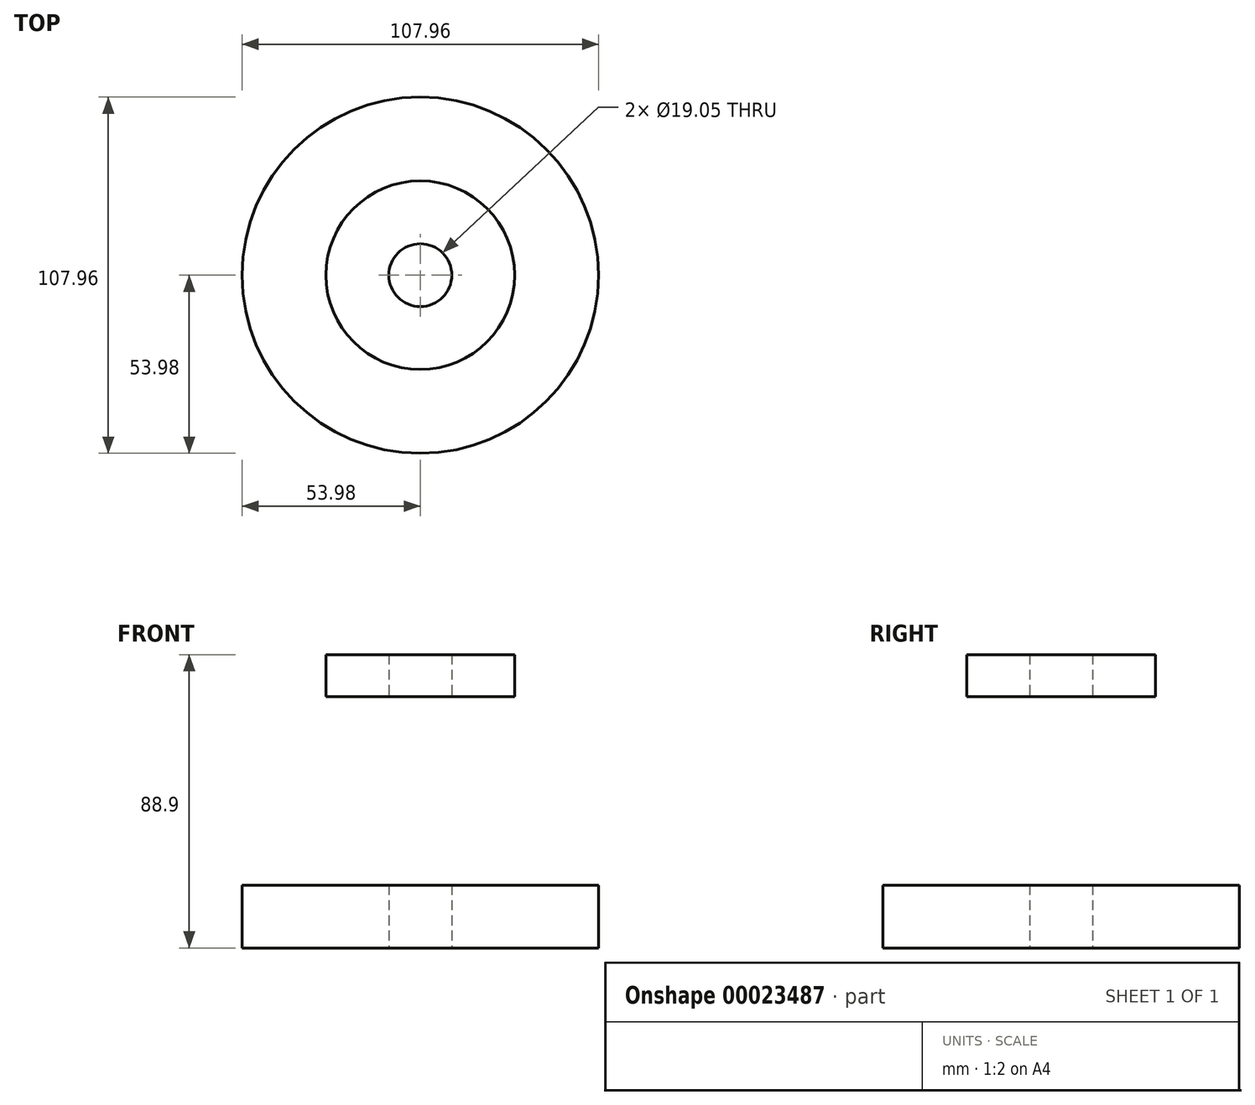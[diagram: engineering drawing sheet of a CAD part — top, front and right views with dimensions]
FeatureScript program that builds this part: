
annotation { "Feature Type Name" : "Feature", "Feature Type Description" : "" }
export const myFeature = defineFeature(function(context is Context, id is Id, definition is map)
    precondition{}
    {
        {
            var Q0;
            Q0=qCreatedBy(makeId("Right.planeOp"),FACE);
            var sketch = newSketch(context, id + "F0", { "sketchPlane" : qUnion([Q0])});
            skLineSegment(sketch, "E0.bottom", {"start": v(0, -35.86) * mm, "end": v(9.53, -35.86) * mm});
            skLineSegment(sketch, "E0.top", {"start": v(0, 53.04) * mm, "end": v(9.52, 53.04) * mm});
            skLineSegment(sketch, "E0.left", {"start": v(0, -35.86) * mm, "end": v(0, 53.04) * mm});
            skLineSegment(sketch, "E0.right", {"start": v(9.53, -35.86) * mm, "end": v(9.52, 53.04) * mm});
            skLineSegment(sketch, "E1.bottom", {"start": v(9.53, -35.86) * mm, "end": v(53.98, -35.86) * mm});
            skLineSegment(sketch, "E1.top", {"start": v(9.52, -16.8) * mm, "end": v(53.98, -16.8) * mm});
            skLineSegment(sketch, "E1.left", {"start": v(9.53, -35.86) * mm, "end": v(9.53, -16.8) * mm});
            skLineSegment(sketch, "E1.right", {"start": v(53.98, -35.86) * mm, "end": v(53.98, -16.8) * mm});
            skLineSegment(sketch, "E2.bottom", {"start": v(9.52, -16.8) * mm, "end": v(34.93, -16.8) * mm});
            skLineSegment(sketch, "E2.top", {"start": v(9.52, 40.34) * mm, "end": v(34.92, 40.34) * mm});
            skLineSegment(sketch, "E2.left", {"start": v(9.52, -16.8) * mm, "end": v(9.52, 40.34) * mm});
            skLineSegment(sketch, "E2.right", {"start": v(34.93, -16.8) * mm, "end": v(34.92, 40.34) * mm});
            skLineSegment(sketch, "E3.top", {"start": v(9.52, 40.34) * mm, "end": v(28.57, 40.34) * mm});
            skLineSegment(sketch, "E3.left", {"start": v(9.52, 53.04) * mm, "end": v(9.52, 40.34) * mm});
            skLineSegment(sketch, "E4.bottom", {"start": v(9.52, 53.04) * mm, "end": v(28.57, 53.04) * mm});
            skLineSegment(sketch, "E4.right", {"start": v(28.57, 53.04) * mm, "end": v(28.57, 40.34) * mm});
            skSolve(sketch);
        }
        {
            var Q0;
            Q0=makeQuery(id+"F0.imprint","IMPRINT",FACE,{"disambiguationData":[TD([[makeQuery(id+"F0.imprint","IMPRINT",EDGE,{"derivedFrom":sQuery(id+"F0.wireOp",EDGE,"E4.bottom")}),-1.0]])]});
            var Q1;
            Q1=makeQuery(id+"F0.imprint","IMPRINT",FACE,{"disambiguationData":[TD([[makeQuery(id+"F0.imprint","IMPRINT",EDGE,{"derivedFrom":sQuery(id+"F0.wireOp",EDGE,"E2.bottom")}),1.0]])]});
            var Q2;
            Q2=makeQuery(id+"F0.imprint","IMPRINT",FACE,{"disambiguationData":[TD([[makeQuery(id+"F0.imprint","IMPRINT",EDGE,{"derivedFrom":sQuery(id+"F0.wireOp",EDGE,"E1.bottom")}),1.0]])]});
            var Q3;
            Q3=sQuery(id+"F0.wireOp",EDGE,"E0.left");
            revolve(context, id + "F1", {"entities" : qUnion([Q0, Q1, Q2]), "axis" : qUnion([Q3]), "revolveType" : RevolveType.FULL});
        }
    });
